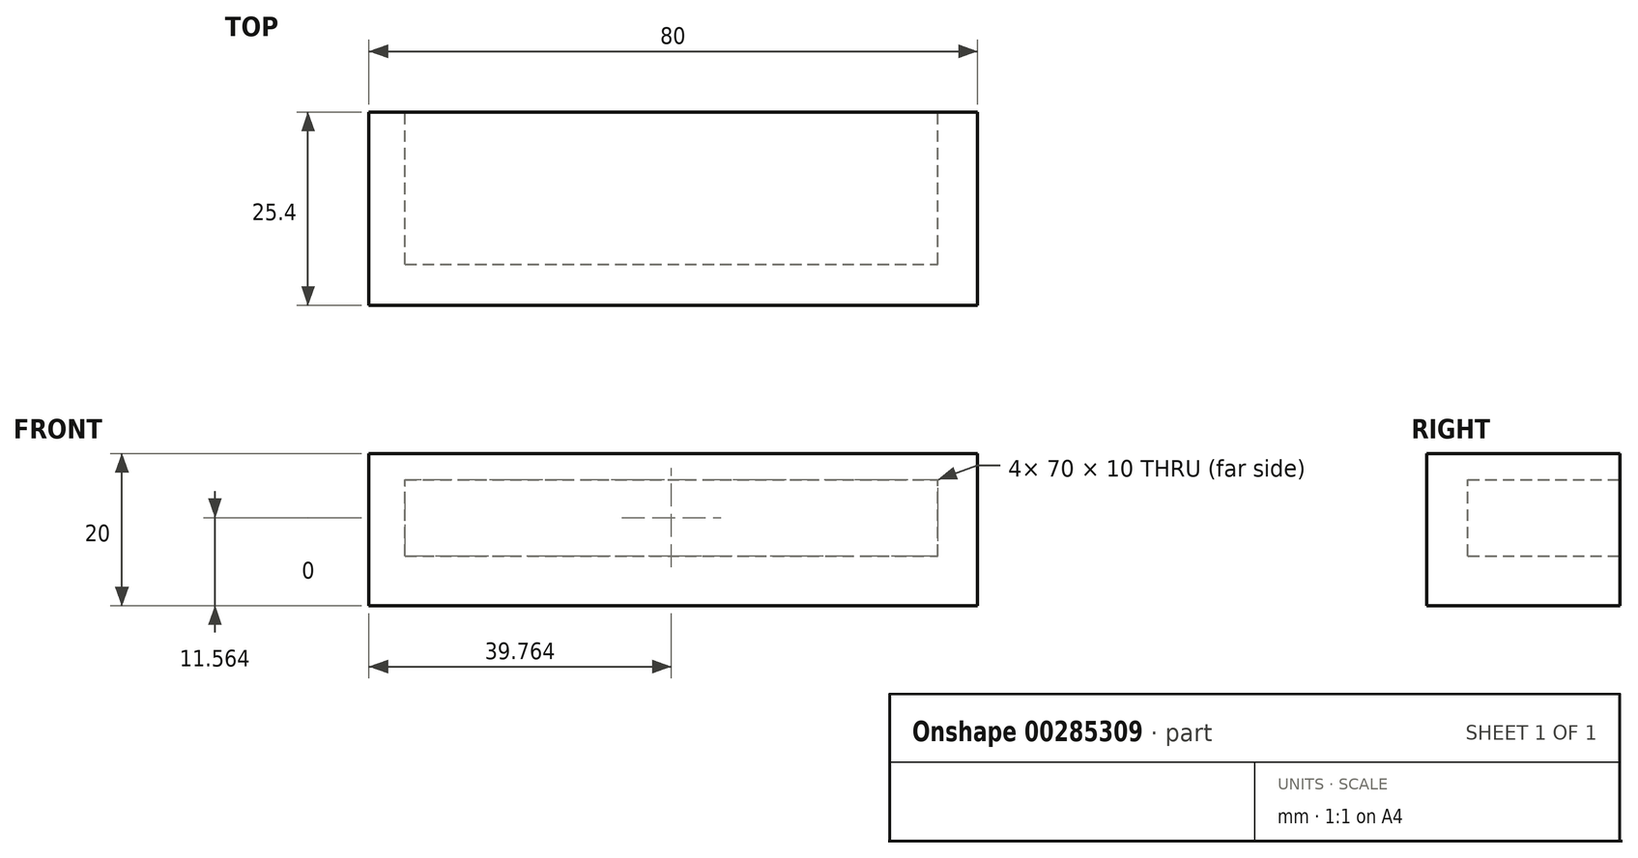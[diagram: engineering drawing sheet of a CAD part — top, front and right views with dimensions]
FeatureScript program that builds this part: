
annotation { "Feature Type Name" : "Feature", "Feature Type Description" : "" }
export const myFeature = defineFeature(function(context is Context, id is Id, definition is map)
    precondition{}
    {
        {
            var Q0;
            Q0=qCreatedBy(makeId("Front.planeOp"),FACE);
            var sketch = newSketch(context, id + "F0", { "sketchPlane" : qUnion([Q0])});
            skLineSegment(sketch, "E0.bottom", {"start": v(0, 0) * mm, "end": v(80, 0) * mm});
            skLineSegment(sketch, "E0.top", {"start": v(0, 20) * mm, "end": v(80, 20) * mm});
            skLineSegment(sketch, "E0.left", {"start": v(0, 0) * mm, "end": v(0, 20) * mm});
            skLineSegment(sketch, "E0.right", {"start": v(80, 0) * mm, "end": v(80, 20) * mm});
            skSolve(sketch);
        }
        {
            var Q0;
            Q0 = qSketchRegion(id + "F0", true);
            extrude(context, id + "F1", {"entities" : qUnion([Q0]), "depth" : 25.4 * mm});
        }
        {
            var Q0;
            Q0=qCreatedBy(makeId("Front.planeOp"),FACE);
            var sketch = newSketch(context, id + "F2", { "sketchPlane" : qUnion([Q0])});
            skLineSegment(sketch, "E1.bottom", {"start": v(4.76, 6.56) * mm, "end": v(74.76, 6.56) * mm});
            skLineSegment(sketch, "E1.top", {"start": v(4.76, 16.56) * mm, "end": v(74.76, 16.56) * mm});
            skLineSegment(sketch, "E1.left", {"start": v(4.76, 6.56) * mm, "end": v(4.76, 16.56) * mm});
            skLineSegment(sketch, "E1.right", {"start": v(74.76, 6.56) * mm, "end": v(74.76, 16.56) * mm});
            skSolve(sketch);
        }
        {
            var Q0;
            Q0=makeQuery(id+"F2.imprint","IMPRINT",FACE,{"disambiguationData":[TD([[makeQuery(id+"F2.imprint","IMPRINT",EDGE,{"derivedFrom":sQuery(id+"F2.wireOp",EDGE,"E1.bottom")}),1.0]])]});
            extrude(context, id + "F3", {"entities" : qUnion([Q0]), "operationType" : NewBodyOperationType.REMOVE, "oppositeDirection" : true, "depth" : 20 * mm});
        }
        {
            var Q0;
            Q0=makeQuery(id+"F2.imprint","IMPRINT",FACE,{"disambiguationData":[TD([[makeQuery(id+"F2.imprint","IMPRINT",EDGE,{"derivedFrom":sQuery(id+"F2.wireOp",EDGE,"E1.bottom")}),1.0]])]});
            extrude(context, id + "F4", {"entities" : qUnion([Q0]), "operationType" : NewBodyOperationType.REMOVE, "depth" : 20 * mm});
        }
    });
